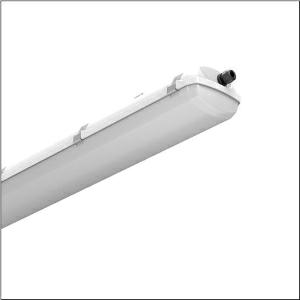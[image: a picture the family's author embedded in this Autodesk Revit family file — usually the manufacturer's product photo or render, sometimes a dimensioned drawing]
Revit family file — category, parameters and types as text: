
# Revit family: monsun_r__ex_51fxa27l860a_0ded
name_source: partatom
category: Lighting Fixtures
units: mm (PartAtom-declared; Revit-internal decimal feet)

## family parameters
Cut with Voids When Loaded = No
Host = Face
Light Source = No
Part Type = Normal
Room Calculation Point = No
Round Connector Dimension = Use Diameter
Shared = No

## types (1)
- Monsun® Ex (1 x LED, 6560 lm, 53 W, 6500K)
    Apparent Load = 53 VA
    CIE Flux Codes = 46 76 94 98 100
    Color Rendering = 80
    Color Temperature = 6500K
    Default Elevation = 1800 mm
    Description = Monsun® Ex, damp-proof luminaire, primary optical cover: cover, of PC, UV-stabilised, opal, light emission: direct distribution, primary light characteristic: symmetric, installation type: surface-mounted, LED, rated luminous flux: 6.560lm, luminous efficacy: 124lm/W, light colour: 860, colour temperature: 6000K, control gear: ECG, with terminal, 3-pole, max. 2.5mm², through-wiring: 5x 2.5mm², mains connection: 220..250V, AC, 50/60Hz, rated input power: 53W, housing, of PC, light grey (RAL 7035), incl. 1x Ex cable gland M20 for cable diameter 7..12mm with sealing, incl. 1x Ex locking screw M20 with sealing, length: 1.280mm, width: 155mm, height: 105mm, clip for enclosure, of stainless steel, protection rating (complete): IP66, insulation class (complete): insulation class I (protective earthing), certification: CE, explosion class: zone 1,21 II 2G Ex eb mb op is IIC T4 Gb, II 2D Ex tb op is IIIC T67°C Db, impact resistance: IK10, permissible operating ambient temperature: -20..+40°C, contact your sales advisor before using the luminaires in applications with unclear chemical exposure, large temperature fluctuations or condensation-forming humidity, packaging unit: 1 piece
    Height = 105 mm
    Lamp = 1 x LED
    Lamp Light Flux = 6560 lm
    Lamp Power = 53 W
    Lamp count = 1
    Length = 1280 mm
    Luminous efficacy = 124 lm/W
    Manufacturer = Siteco
    ModVariant = No
    Model = 51FXA27L860A
    Mounting Place = Ceiling
    Mounting Type = Surface mounted
    Number of Poles = 1
    OnlyDefault = Yes
    Power Factor = 1
    Product Name = Monsun® Ex
    Product group = damp-proof luminaire
    ProductGroupID = 301
    Protection Class = Protection class I
    Protection Degree = IP 66
    RLX_Detail_Level = 1
    RLX_Emergency_Light_Flux = 0 lm
    RLX_Emergency_Type = 0
    RLX_Emergency_Type_DB = No
    RlxData = <blob elided: 41773 chars, md5=c6975350>
    Socket = socket
    Standby Power = 0 W
    System Light Flux = 6560 lm
    System Power = 53 W
    Type Comments = Product without accessories
    Type Image = l_1258882.jpg
    URL = http://relux.com
    VarID = ---
    Voltage = 0 V
    Weight = 0.00 kg
    Width = 155 mm

## geometry (parser evidence)
native form markers: Blend x4, Sweep x9
no freeform markers — native parametric forms only
